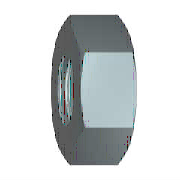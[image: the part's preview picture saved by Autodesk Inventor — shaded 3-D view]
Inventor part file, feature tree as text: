
AUTODESK INVENTOR PART (.ipt)
format: ipt  version: 2020 (Build 240168000, 168)  size: 164,864 bytes
history: native  units: mm (DEFAULTED — no unit token found)
features: sketch x3, chamfer x1, hole x1, other x1, plane x1
ambient origin geometry x7: Origin, YZ Plane, XZ Plane, X Axis, Y Axis, Z Axis, Center Point
bodies: Solid1 (feature_tree), Body (feature_tree)
feature tree (7):
  chamfer  "Chamfer1"  Angle=30.0deg  [1 undecoded]
  hole  "Thread"  [1 undecoded]
  other  "Work Axis1"
  plane  "Work Plane1"
  sketch  "Sketch1"  dims[d0=11.547005mm]
  sketch  "Sketch2"  dims[d1=5.0mm]
  sketch  "Sketch3"  dims[d2=0.0mm d3=30.0deg d4=30.0deg d5=8.7mm d6=8.7mm d7=90.0deg d25=4.917mm d26=6.0mm d27=4.0mm d28=2.0mm d29=14.3117mm d30=8.0mm d31=20.594885mm d8=0.541266mm d9=30.0deg d10=0.541266mm d11=30.0deg d13=0.0mm d14=0.0mm d39=0.0mm d40=0.541266mm d41=0.541266mm d42=0.0mm]
note: 2 required parameter values undecoded (feature->parameter linkage not recoverable at this tier; creation-order binding heuristic only, values carry confidence <= 0.55)
